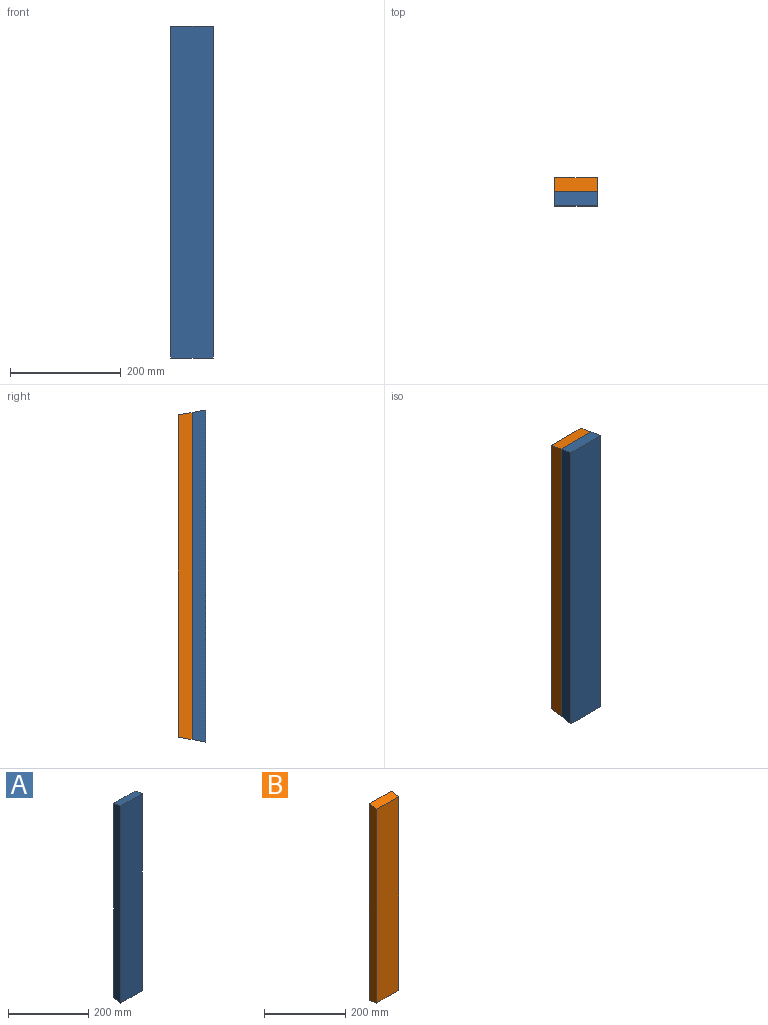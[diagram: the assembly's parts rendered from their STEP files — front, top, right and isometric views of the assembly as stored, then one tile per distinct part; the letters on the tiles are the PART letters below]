
ASSEMBLY  parts=2 mates=1
PART A: 6 faces, bbox 76x25x600 mm
  f0: plane 600x25mm, normal (-1,0,0), area 14889.8mm2, adj f1,f3,f4,f5
  f1: plane 591.18x76mm, normal (0,1,0), area 44930mm2, adj f0,f2,f4,f5
  f2: plane 600x25mm, normal (1,0,0), area 14889.8mm2, adj f1,f3,f4,f5
  f3: plane 600x76mm, normal (0,-1,0), area 45600mm2, adj f0,f2,f4,f5
  f4: plane 76x25mm, normal (0,0.17,-0.98), area 1929.3mm2, adj f0,f1,f2,f3
  f5: plane 76x25mm, normal (0,0.17,0.98), area 1929.3mm2, adj f0,f1,f2,f3
PART B: 6 faces, bbox 76x25x591.2 mm
  f0: plane 582.38x76mm, normal (0,-1,0), area 44261.2mm2, adj f1,f2,f4,f5
  f1: plane 591.2x25mm, normal (-1,0,0), area 14669.8mm2, adj f0,f3,f4,f5
  f2: plane 591.2x25mm, normal (1,0,0), area 14669.8mm2, adj f0,f3,f4,f5
  f3: plane 591.2x76mm, normal (0,1,0), area 44931.2mm2, adj f1,f2,f4,f5
  f4: plane 76x25mm, normal (0,-0.17,-0.98), area 1929.3mm2, adj f0,f1,f2,f3
  f5: plane 76x25mm, normal (0,-0.17,0.98), area 1929.3mm2, adj f0,f1,f2,f3
PLACE A t=(-138.79,10.6,14.32)mm
PLACE B rot(axis=(0,0,1),180deg) t=(279.98,10.6,14.31)mm
MATE fastened B.f3 <-> A.f1  axis (0,-1,0) through (51.29,10.6,281.23)mm
